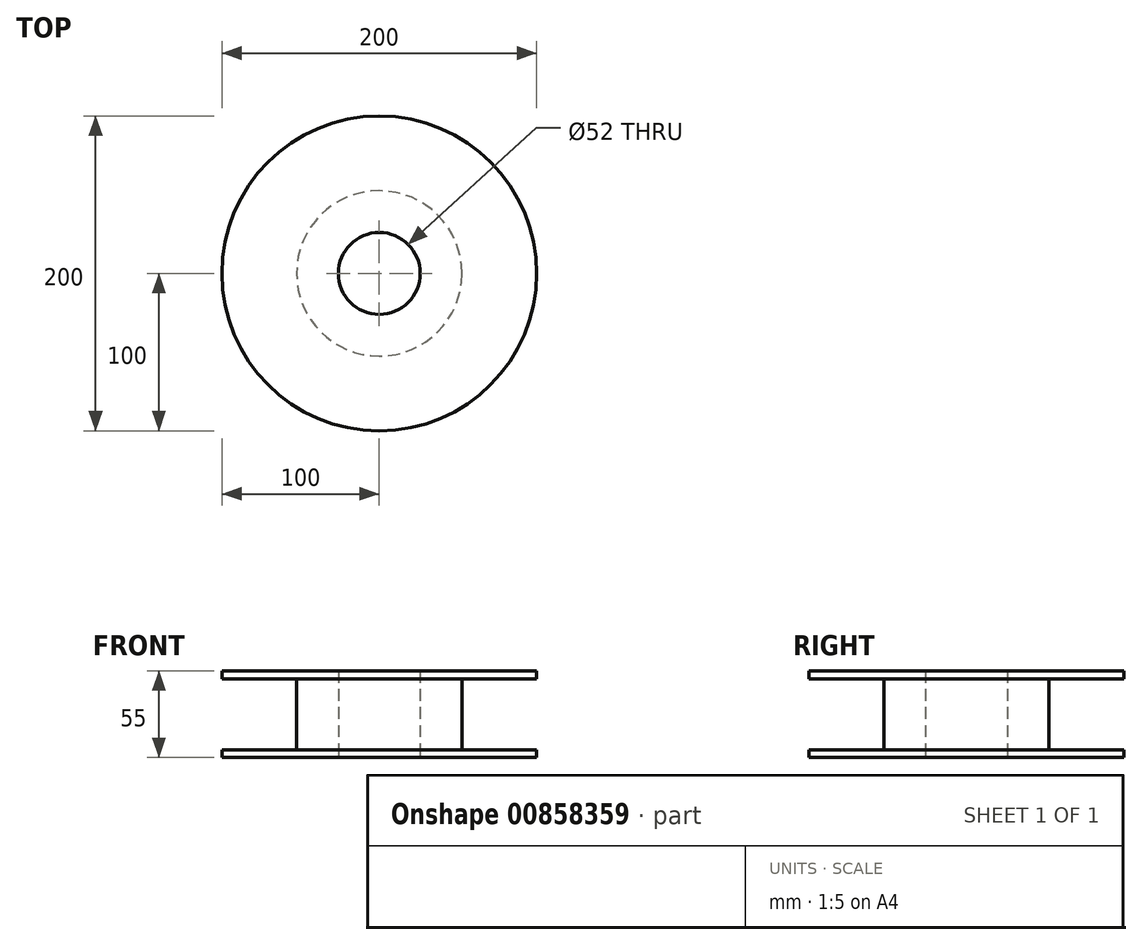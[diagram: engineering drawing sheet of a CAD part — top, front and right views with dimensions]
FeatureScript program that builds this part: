
annotation { "Feature Type Name" : "Feature", "Feature Type Description" : "" }
export const myFeature = defineFeature(function(context is Context, id is Id, definition is map)
    precondition{}
    {
        {
            var Q0;
            Q0=qCreatedBy(makeId("Front.planeOp"),FACE);
            var sketch = newSketch(context, id + "F0", { "sketchPlane" : qUnion([Q0])});
            skLineSegment(sketch, "E0", {"start": v(-100, 27.5) * mm, "end": v(-100, 22.5) * mm});
            skLineSegment(sketch, "E1", {"start": v(-100, 22.5) * mm, "end": v(-52.5, 22.5) * mm});
            skLineSegment(sketch, "E2", {"start": v(-52.5, 22.5) * mm, "end": v(-52.5, -22.5) * mm});
            skLineSegment(sketch, "E3", {"start": v(-52.5, -22.5) * mm, "end": v(-100, -22.5) * mm});
            skLineSegment(sketch, "E4", {"start": v(-100, -22.5) * mm, "end": v(-100, -27.5) * mm});
            skLineSegment(sketch, "E5", {"start": v(-100, -27.5) * mm, "end": v(-26, -27.5) * mm});
            skLineSegment(sketch, "E6", {"start": v(-100, 27.5) * mm, "end": v(-26, 27.5) * mm});
            skLineSegment(sketch, "E7", {"start": v(-26, 27.5) * mm, "end": v(-26, -27.5) * mm});
            skLineSegment(sketch, "E8", {"start": v(0, -36.61) * mm, "end": v(0, 31.36) * mm, "construction": true});
            skSolve(sketch);
        }
        {
            var Q0;
            Q0=makeQuery(id+"F0.imprint","IMPRINT",FACE,{"disambiguationData":[TD([[makeQuery(id+"F0.imprint","IMPRINT",EDGE,{"derivedFrom":sQuery(id+"F0.wireOp",EDGE,"E0")}),1.0]])]});
            var Q1;
            Q1=qConstructionFilter(qBodyType(qCreatedBy(id+"F0",EDGE),BodyType.WIRE),ConstructionObject.NO);
            var Q2;
            Q2=sQuery(id+"F0.wireOp",EDGE,"E8");
            revolve(context, id + "F1", {"surfaceOperationType" : NewSurfaceOperationType.NEW, "entities" : qUnion([Q0]), "surfaceEntities" : qUnion([Q1]), "axis" : qUnion([Q2]), "revolveType" : RevolveType.FULL});
        }
    });
